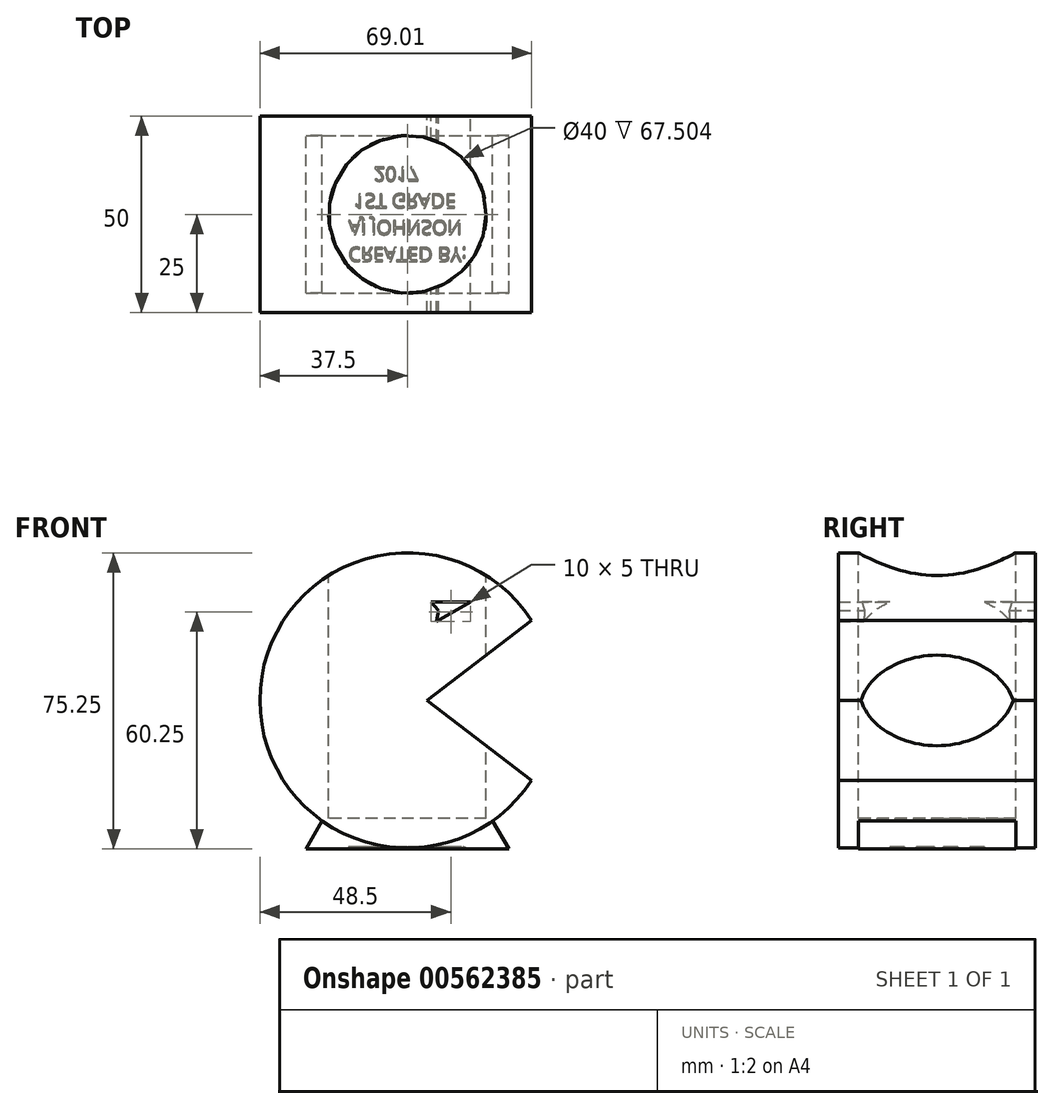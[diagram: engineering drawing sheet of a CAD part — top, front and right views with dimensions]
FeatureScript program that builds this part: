
annotation { "Feature Type Name" : "Feature", "Feature Type Description" : "" }
export const myFeature = defineFeature(function(context is Context, id is Id, definition is map)
    precondition{}
    {
        {
            var Q0;
            Q0=qCreatedBy(makeId("Front.planeOp"),FACE);
            var sketch = newSketch(context, id + "F0", { "sketchPlane" : qUnion([Q0])});
            skArc(sketch, "E0", {"start": v(31.5, 20.34) * mm, "mid": v(-37.5, 0) * mm, "end": v(31.5, -20.34) * mm});
            skLineSegment(sketch, "E1", {"start": v(31.5, 20.34) * mm, "end": v(5, 0) * mm});
            skLineSegment(sketch, "E2", {"start": v(5, 0) * mm, "end": v(31.5, -20.34) * mm});
            skLineSegment(sketch, "E3", {"start": v(16, 25) * mm, "end": v(6, 25) * mm});
            skLineSegment(sketch, "E4", {"start": v(6, 25) * mm, "end": v(7.84, 22.81) * mm});
            skLineSegment(sketch, "E5", {"start": v(7.84, 22.81) * mm, "end": v(7.34, 20) * mm});
            skLineSegment(sketch, "E6", {"start": v(7.34, 20) * mm, "end": v(16, 25) * mm});
            skLineSegment(sketch, "E7", {"start": v(-21.65, -30.62) * mm, "end": v(-25.76, -37.75) * mm});
            skLineSegment(sketch, "E8", {"start": v(-25.76, -37.75) * mm, "end": v(25.76, -37.75) * mm});
            skLineSegment(sketch, "E9", {"start": v(25.76, -37.75) * mm, "end": v(21.65, -30.62) * mm});
            skSolve(sketch);
        }
        {
            var Q0;
            {var subQ0=sQuery(id+"F0.wireOp",EDGE,"E1");Q0=makeQuery(id+"F0.imprint","IMPRINT",FACE,{"disambiguationData":[TD([[makeQuery(id+"F0.imprint","IMPRINT",EDGE,{"derivedFrom":subQ0}),-1.0]])]});}
            extrude(context, id + "F1", {"entities" : qUnion([Q0]), "endBound" : BoundingType.SYMMETRIC, "depth" : 50 * mm, "offsetDistance" : 25 * mm});
        }
        {
            var Q0;
            {var subQ0=sQuery(id+"F0.wireOp",EDGE,"E7");Q0=makeQuery(id+"F0.imprint","IMPRINT",FACE,{"disambiguationData":[TD([[makeQuery(id+"F0.imprint","IMPRINT",EDGE,{"derivedFrom":subQ0}),1.0]])]});}
            extrude(context, id + "F2", {"entities" : qUnion([Q0]), "operationType" : NewBodyOperationType.ADD, "endBound" : BoundingType.SYMMETRIC, "depth" : 40 * mm, "offsetDistance" : 25 * mm});
        }
        {
            var Q0;
            Q0=qCreatedBy(makeId("Top.planeOp"),FACE);
            var sketch = newSketch(context, id + "F3", { "sketchPlane" : qUnion([Q0])});
            skCircle(sketch, "E10", {"center": v(0, 0) * mm, "radius": 20 * mm});
            skSolve(sketch);
        }
        {
            var Q0;
            Q0 = qSketchRegion(id + "F3", true);
            extrude(context, id + "F4", {"entities" : qUnion([Q0]), "operationType" : NewBodyOperationType.REMOVE, "oppositeDirection" : true, "depth" : 30 * mm, "offsetDistance" : 25 * mm, "hasSecondDirection" : true, "secondDirectionBound" : SecondDirectionBoundingType.THROUGH_ALL, "secondDirectionOppositeDirection" : false, "secondDirectionDepth" : 25 * mm});
        }
        {
            var Q0;
            Q0=makeQuery(id+"F2.opExtrude","SWEPT_FACE",FACE,{"disambiguationData":[OSD([sQuery(id+"F0.wireOp",EDGE,"E8")])]});
            var sketch = newSketch(context, id + "F5", { "sketchPlane" : qUnion([Q0])});
            skText(sketch, "E11", { "text": "CREATED BY:\nAJ JOHNSON\n 1ST GRADE\n     2017", "fontName": "OpenSans-Regular.ttf"});
            const initialGuessF5  = {"E11": [-0.015, 0.0084, 1, 0, 0.0036]};
            skSetInitialGuess(sketch, initialGuessF5);
            skSolve(sketch);
        }
        {
            var Q0;
            Q0 = qSketchRegion(id + "F5", true);
            extrude(context, id + "F6", {"entities" : qUnion([Q0]), "operationType" : NewBodyOperationType.REMOVE, "oppositeDirection" : true, "depth" : .5 * mm, "offsetDistance" : 25 * mm});
        }
    });
